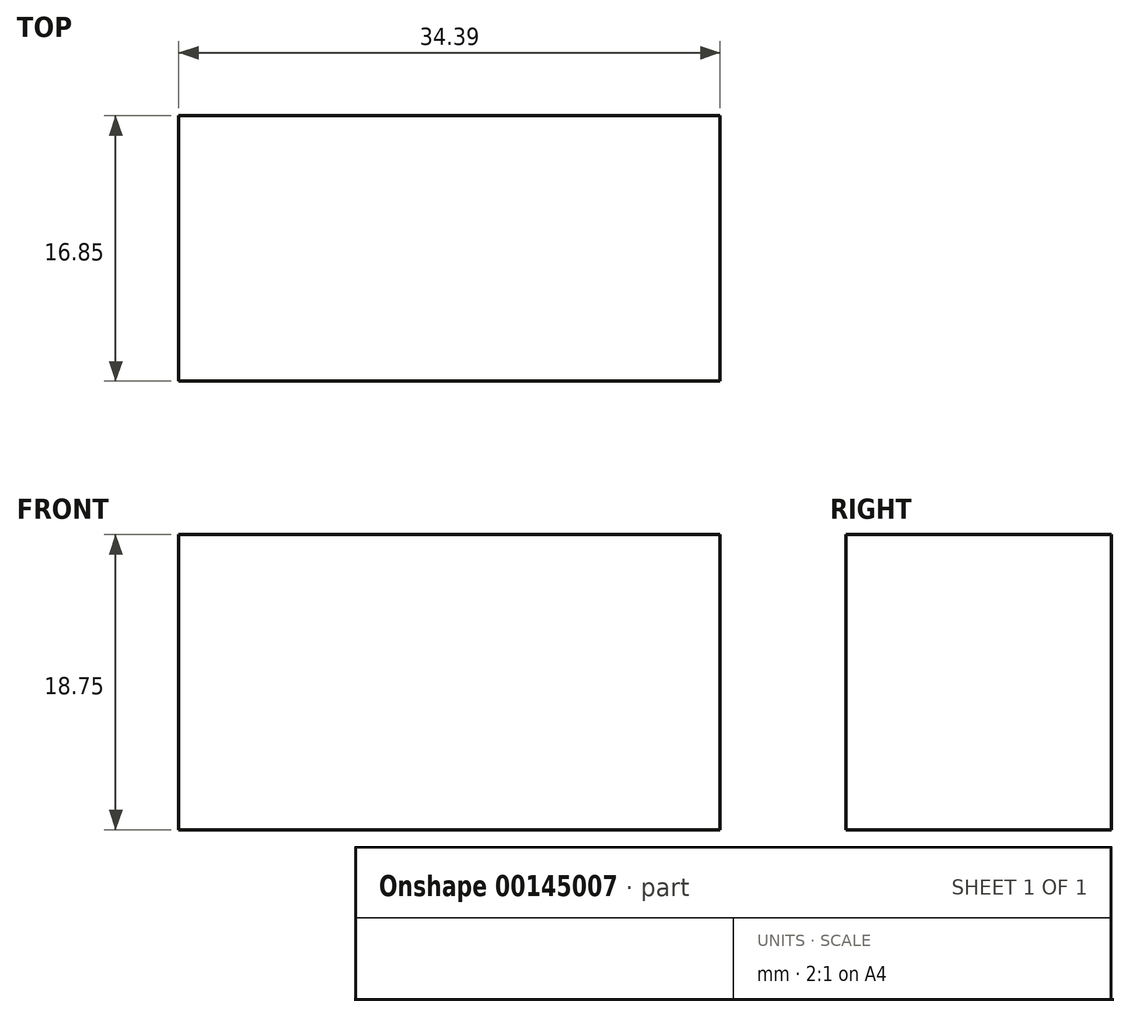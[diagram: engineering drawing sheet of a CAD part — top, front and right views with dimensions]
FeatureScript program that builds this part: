
annotation { "Feature Type Name" : "Feature", "Feature Type Description" : "" }
export const myFeature = defineFeature(function(context is Context, id is Id, definition is map)
    precondition{}
    {
        {
            var Q0;
            Q0=qCreatedBy(makeId("Right.planeOp"),FACE);
            var sketch = newSketch(context, id + "F0", { "sketchPlane" : qUnion([Q0])});
            skLineSegment(sketch, "E0.bottom", {"start": v(-43.48, 0) * mm, "end": v(-26.63, 0) * mm});
            skLineSegment(sketch, "E0.top", {"start": v(-43.48, 18.75) * mm, "end": v(-26.63, 18.75) * mm});
            skLineSegment(sketch, "E0.left", {"start": v(-43.48, 0) * mm, "end": v(-43.48, 18.75) * mm});
            skLineSegment(sketch, "E0.right", {"start": v(-26.63, 0) * mm, "end": v(-26.63, 18.75) * mm});
            skSolve(sketch);
        }
        {
            var Q0;
            Q0 = qSketchRegion(id + "F0", true);
            extrude(context, id + "F1", {"entities" : qUnion([Q0]), "depth" : 34.4 * mm});
        }
    });
